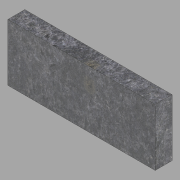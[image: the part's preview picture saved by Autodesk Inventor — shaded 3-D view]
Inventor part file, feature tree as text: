
AUTODESK INVENTOR PART (.ipt)
format: ipt  version: 2022.2 (Build 262287000, 287)  size: 115,712 bytes
history: native  units: in
note: dims shown in document units (in); Inventor stores cm internally (conversion verified against a paired STEP export)
features: extrude x1, sketch x1
ambient origin geometry x8: Origin, YZ Plane, XZ Plane, XY Plane, X Axis, Y Axis, Z Axis, Center Point
bodies: Solid1 (feature_tree)
feature tree (2):
  extrude  "Extrusion1"  Depth=7.625in
  sketch  "Sketch1"  dims[d0=2.25in d1=7.625in d2=19.625in d3=0.0in]
